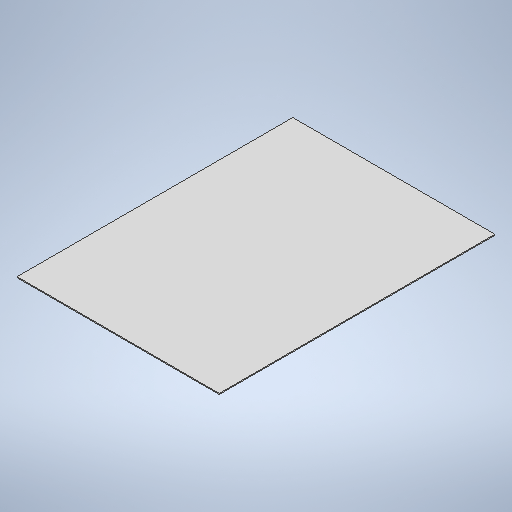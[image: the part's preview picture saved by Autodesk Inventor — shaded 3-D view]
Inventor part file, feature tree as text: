
AUTODESK INVENTOR PART (.ipt)
format: ipt  version: 2025.1 (Build 291241000, 241)  size: 200,192 bytes
history: native  units: mm
features: extrude x1, sketch x1
ambient origin geometry x8: Origin, YZ Plane, XZ Plane, XY Plane, X Axis, Y Axis, Z Axis, Center Point
bodies: Solide1 (feature_tree)
feature tree (2):
  extrude  "Extrusion1"  Depth=220.0mm
  sketch  "Esquisse1"
